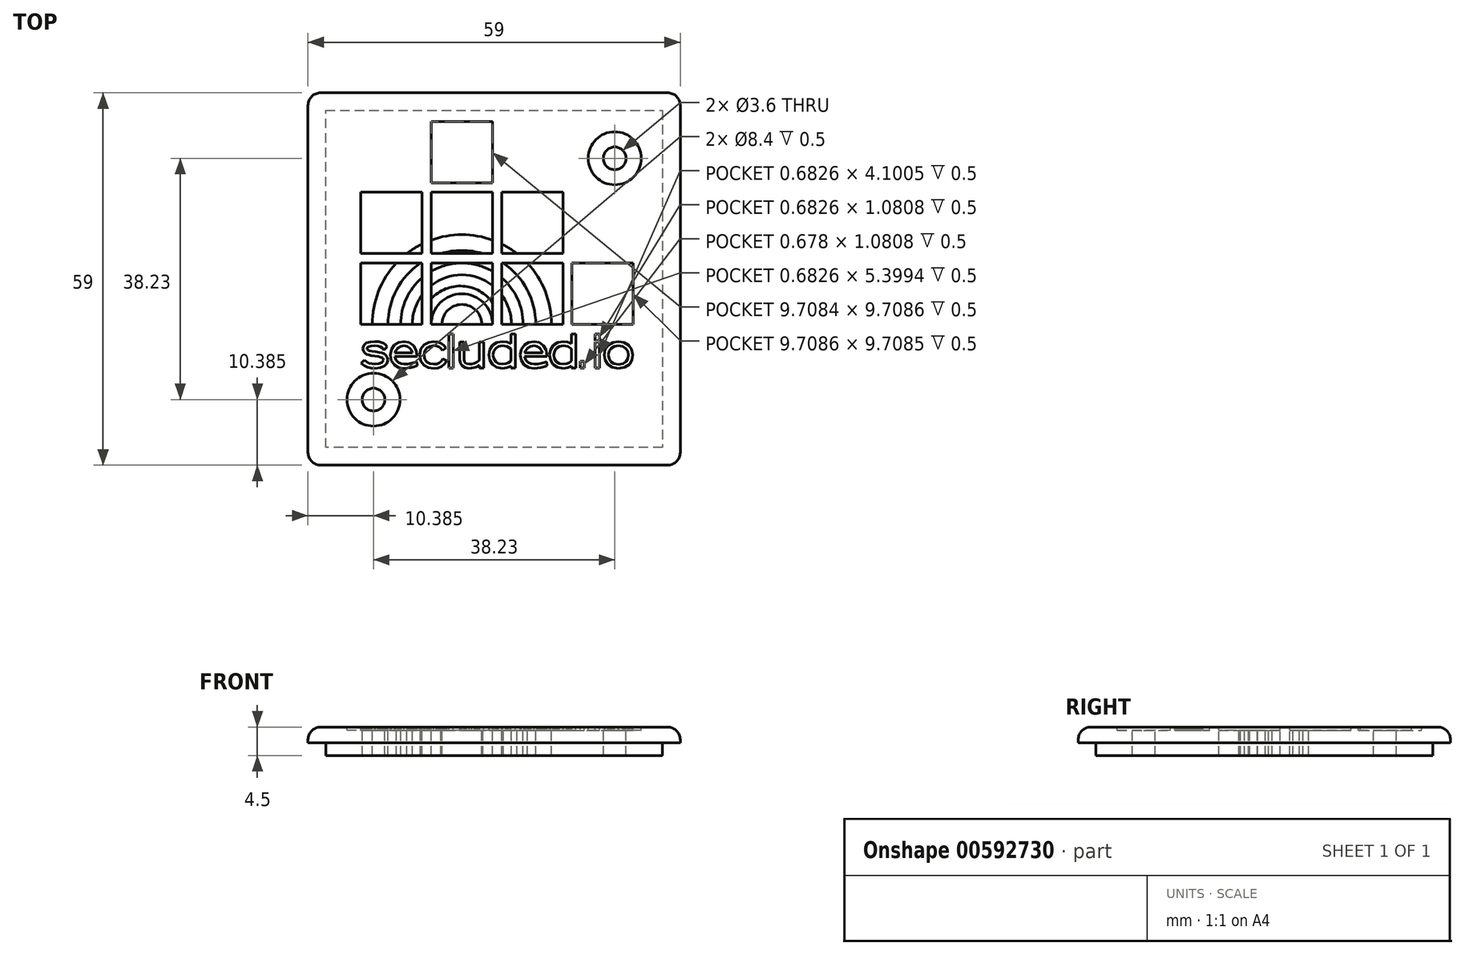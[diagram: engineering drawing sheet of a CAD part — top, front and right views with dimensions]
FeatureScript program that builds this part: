
annotation { "Feature Type Name" : "Feature", "Feature Type Description" : "" }
export const myFeature = defineFeature(function(context is Context, id is Id, definition is map)
    precondition{}
    {
        {
            var Q0;
            Q0=qCreatedBy(makeId("Top.planeOp"),FACE);
            var sketch = newSketch(context, id + "F0", { "sketchPlane" : qUnion([Q0])});
            skLineSegment(sketch, "E0.bottom", {"start": v(29.5, 29.5) * mm, "end": v(-29.5, 29.5) * mm});
            skLineSegment(sketch, "E0.top", {"start": v(29.5, -29.5) * mm, "end": v(-29.5, -29.5) * mm});
            skLineSegment(sketch, "E0.left", {"start": v(29.5, 29.5) * mm, "end": v(29.5, -29.5) * mm});
            skLineSegment(sketch, "E0.right", {"start": v(-29.5, 29.5) * mm, "end": v(-29.5, -29.5) * mm});
            skPoint(sketch, "E0.middle", {"position": v(0, 0) * mm});
            skLineSegment(sketch, "E1.bottom", {"start": v(23.88, -23.87) * mm, "end": v(-23.87, -23.88) * mm, "construction": true});
            skLineSegment(sketch, "E1.top", {"start": v(23.88, 23.88) * mm, "end": v(-23.88, 23.88) * mm, "construction": true});
            skLineSegment(sketch, "E1.left", {"start": v(23.88, -23.87) * mm, "end": v(23.88, 23.88) * mm, "construction": true});
            skLineSegment(sketch, "E1.right", {"start": v(-23.87, -23.88) * mm, "end": v(-23.88, 23.88) * mm, "construction": true});
            skSolve(sketch);
        }
        {
            var Q0;
            Q0=makeQuery(id+"F0.imprint","IMPRINT",FACE,{"disambiguationData":[TD([[makeQuery(id+"F0.imprint","IMPRINT",EDGE,{"derivedFrom":sQuery(id+"F0.wireOp",EDGE,"E0.bottom")}),1.0]])]});
            extrude(context, id + "F1", {"entities" : qUnion([Q0]), "depth" : 2.5 * mm, "offsetDistance" : 25 * mm});
        }
        {
            var Q0;
            Q0=makeQuery(id+"F1.opExtrude","CAP_FACE",FACE,{"disambiguationData":[OSD([sQuery(id+"F0.wireOp",EDGE,"E0.bottom"),sQuery(id+"F0.wireOp",EDGE,"E0.top"),sQuery(id+"F0.wireOp",EDGE,"E0.left"),sQuery(id+"F0.wireOp",EDGE,"E0.right")])],"isStart":true});
            var sketch = newSketch(context, id + "F2", { "sketchPlane" : qUnion([Q0])});
            skLineSegment(sketch, "E2.0", {"start": v(26.7, -26.7) * mm, "end": v(26.7, 26.7) * mm});
            skLineSegment(sketch, "E2.1", {"start": v(-26.7, -26.7) * mm, "end": v(26.7, -26.7) * mm});
            skLineSegment(sketch, "E2.2", {"start": v(-26.7, 26.7) * mm, "end": v(-26.7, -26.7) * mm});
            skLineSegment(sketch, "E2.3", {"start": v(26.7, 26.7) * mm, "end": v(-26.7, 26.7) * mm});
            skSolve(sketch);
        }
        {
            var Q0;
            Q0 = qSketchRegion(id + "F2", true);
            extrude(context, id + "F3", {"entities" : qUnion([Q0]), "operationType" : NewBodyOperationType.ADD, "depth" : 2 * mm, "offsetDistance" : 25 * mm});
        }
        {
            var Q0;
            Q0=makeQuery(id+"F1.opExtrude","CAP_FACE",FACE,{"disambiguationData":[OSD([sQuery(id+"F0.wireOp",EDGE,"E0.bottom"),sQuery(id+"F0.wireOp",EDGE,"E0.top"),sQuery(id+"F0.wireOp",EDGE,"E0.left"),sQuery(id+"F0.wireOp",EDGE,"E0.right")])],"isStart":false});
            var sketch = newSketch(context, id + "F4", { "sketchPlane" : qUnion([Q0])});
            skCircle(sketch, "E3", {"center": v(19.11, 19.12) * mm, "radius": 1.8 * mm});
            skCircle(sketch, "E4", {"center": v(-19.11, -19.11) * mm, "radius": 1.8 * mm});
            skSolve(sketch);
        }
        {
            var Q0;
            Q0 = qSketchRegion(id + "F4", true);
            extrude(context, id + "F5", {"entities" : qUnion([Q0]), "operationType" : NewBodyOperationType.REMOVE, "endBound" : BoundingType.THROUGH_ALL, "oppositeDirection" : true, "depth" : 25 * mm, "offsetDistance" : 25 * mm});
        }
        {
            var Q0;
            Q0=makeQuery(id+"F1.opExtrude","SWEPT_EDGE",EDGE,{"disambiguationData":[OSD([sQuery(id+"F0.wireOp",EDGE,"E0.top"),sQuery(id+"F0.wireOp",EDGE,"E0.right")])]});
            var Q1;
            Q1=makeQuery(id+"F1.opExtrude","SWEPT_EDGE",EDGE,{"disambiguationData":[OSD([sQuery(id+"F0.wireOp",EDGE,"E0.top"),sQuery(id+"F0.wireOp",EDGE,"E0.left")])]});
            var Q2;
            Q2=makeQuery(id+"F1.opExtrude","SWEPT_EDGE",EDGE,{"disambiguationData":[OSD([sQuery(id+"F0.wireOp",EDGE,"E0.bottom"),sQuery(id+"F0.wireOp",EDGE,"E0.left")])]});
            var Q3;
            Q3=makeQuery(id+"F1.opExtrude","SWEPT_EDGE",EDGE,{"disambiguationData":[OSD([sQuery(id+"F0.wireOp",EDGE,"E0.bottom"),sQuery(id+"F0.wireOp",EDGE,"E0.right")])]});
            fillet(context, id + "F6", {"entities" : qUnion([Q0, Q1, Q2, Q3]), "radius" : 2 * mm, "tangentPropagation" : true, "allowEdgeOverflow" : false});
        }
        {
            var Q0;
            Q0=makeQuery(id+"F1.opExtrude","CAP_EDGE",EDGE,{"disambiguationData":[OSD([sQuery(id+"F0.wireOp",EDGE,"E0.right")])],"isStart":false});
            fillet(context, id + "F7", {"entities" : qUnion([Q0]), "radius" : 2 * mm, "tangentPropagation" : true, "allowEdgeOverflow" : false});
        }
        {
            var Q0;
            Q0=makeQuery(id+"F1.opExtrude","CAP_FACE",FACE,{"disambiguationData":[OSD([sQuery(id+"F0.wireOp",EDGE,"E0.bottom"),sQuery(id+"F0.wireOp",EDGE,"E0.top"),sQuery(id+"F0.wireOp",EDGE,"E0.left"),sQuery(id+"F0.wireOp",EDGE,"E0.right")])],"isStart":false});
            var sketch = newSketch(context, id + "F8", { "sketchPlane" : qUnion([Q0])});
            skCircle(sketch, "E5", {"center": v(19.11, 19.12) * mm, "radius": 4.2 * mm});
            skCircle(sketch, "E6", {"center": v(-19.11, -19.11) * mm, "radius": 4.2 * mm});
            skSolve(sketch);
        }
        {
            var Q0;
            Q0 = qSketchRegion(id + "F8", true);
            extrude(context, id + "F9", {"entities" : qUnion([Q0]), "operationType" : NewBodyOperationType.REMOVE, "oppositeDirection" : true, "depth" : .5 * mm, "offsetDistance" : 25 * mm});
        }
        {
            var Q0;
            Q0=makeQuery(id+"F1.opExtrude","CAP_FACE",FACE,{"disambiguationData":[OSD([sQuery(id+"F0.wireOp",EDGE,"E0.bottom"),sQuery(id+"F0.wireOp",EDGE,"E0.top"),sQuery(id+"F0.wireOp",EDGE,"E0.left"),sQuery(id+"F0.wireOp",EDGE,"E0.right")])],"isStart":false});
            var sketch = newSketch(context, id + "F10", { "sketchPlane" : qUnion([Q0])});
            skLineSegment(sketch, "E7", {"start": v(-16.85, -12.84) * mm, "end": v(-16.95, -12.39) * mm});
            skLineSegment(sketch, "E8", {"start": v(-16.95, -12.39) * mm, "end": v(-17.23, -12.02) * mm});
            skLineSegment(sketch, "E9", {"start": v(-17.23, -12.02) * mm, "end": v(-17.48, -11.85) * mm});
            skLineSegment(sketch, "E10", {"start": v(-17.48, -11.85) * mm, "end": v(-17.8, -11.73) * mm});
            skLineSegment(sketch, "E11", {"start": v(-17.8, -11.73) * mm, "end": v(-18.23, -11.63) * mm});
            skLineSegment(sketch, "E12", {"start": v(-18.23, -11.63) * mm, "end": v(-18.78, -11.53) * mm});
            skLineSegment(sketch, "E13", {"start": v(-18.78, -11.53) * mm, "end": v(-19.36, -11.44) * mm});
            skLineSegment(sketch, "E14", {"start": v(-19.36, -11.44) * mm, "end": v(-19.71, -11.37) * mm});
            skLineSegment(sketch, "E15", {"start": v(-19.71, -11.37) * mm, "end": v(-19.9, -11.3) * mm});
            skLineSegment(sketch, "E16", {"start": v(-19.9, -11.3) * mm, "end": v(-20.03, -11.22) * mm});
            skLineSegment(sketch, "E17", {"start": v(-20.03, -11.22) * mm, "end": v(-20.12, -11.12) * mm});
            skLineSegment(sketch, "E18", {"start": v(-20.12, -11.12) * mm, "end": v(-20.14, -11.02) * mm});
            skLineSegment(sketch, "E19", {"start": v(-20.14, -11.02) * mm, "end": v(-20.1, -10.87) * mm});
            skLineSegment(sketch, "E20", {"start": v(-20.1, -10.87) * mm, "end": v(-19.93, -10.74) * mm});
            skLineSegment(sketch, "E21", {"start": v(-19.93, -10.74) * mm, "end": v(-19.48, -10.61) * mm});
            skLineSegment(sketch, "E22", {"start": v(-19.48, -10.61) * mm, "end": v(-18.9, -10.58) * mm});
            skLineSegment(sketch, "E23", {"start": v(-18.9, -10.58) * mm, "end": v(-18.4, -10.62) * mm});
            skLineSegment(sketch, "E24", {"start": v(-18.4, -10.62) * mm, "end": v(-18, -10.75) * mm});
            skLineSegment(sketch, "E25", {"start": v(-18, -10.75) * mm, "end": v(-17.7, -10.95) * mm});
            skLineSegment(sketch, "E26", {"start": v(-17.7, -10.95) * mm, "end": v(-17.46, -11.24) * mm});
            skLineSegment(sketch, "E27", {"start": v(-17.46, -11.24) * mm, "end": v(-16.92, -10.78) * mm});
            skLineSegment(sketch, "E28", {"start": v(-16.92, -10.78) * mm, "end": v(-17.15, -10.52) * mm});
            skLineSegment(sketch, "E29", {"start": v(-17.15, -10.52) * mm, "end": v(-17.35, -10.33) * mm});
            skLineSegment(sketch, "E30", {"start": v(-17.35, -10.33) * mm, "end": v(-17.54, -10.2) * mm});
            skLineSegment(sketch, "E31", {"start": v(-17.54, -10.2) * mm, "end": v(-17.72, -10.1) * mm});
            skLineSegment(sketch, "E32", {"start": v(-17.72, -10.1) * mm, "end": v(-18.3, -9.95) * mm});
            skLineSegment(sketch, "E33", {"start": v(-18.3, -9.95) * mm, "end": v(-18.9, -9.91) * mm});
            skLineSegment(sketch, "E34", {"start": v(-18.9, -9.91) * mm, "end": v(-19.63, -9.97) * mm});
            skLineSegment(sketch, "E35", {"start": v(-19.63, -9.97) * mm, "end": v(-20.22, -10.14) * mm});
            skLineSegment(sketch, "E36", {"start": v(-20.22, -10.14) * mm, "end": v(-20.67, -10.48) * mm});
            skLineSegment(sketch, "E37", {"start": v(-20.67, -10.48) * mm, "end": v(-20.83, -11.02) * mm});
            skLineSegment(sketch, "E38", {"start": v(-20.83, -11.02) * mm, "end": v(-20.72, -11.45) * mm});
            skLineSegment(sketch, "E39", {"start": v(-20.72, -11.45) * mm, "end": v(-20.41, -11.78) * mm});
            skLineSegment(sketch, "E40", {"start": v(-20.41, -11.78) * mm, "end": v(-20.17, -11.93) * mm});
            skLineSegment(sketch, "E41", {"start": v(-20.17, -11.93) * mm, "end": v(-19.87, -12.03) * mm});
            skLineSegment(sketch, "E42", {"start": v(-19.87, -12.03) * mm, "end": v(-19.47, -12.12) * mm});
            skLineSegment(sketch, "E43", {"start": v(-19.47, -12.12) * mm, "end": v(-18.92, -12.2) * mm});
            skLineSegment(sketch, "E44", {"start": v(-18.92, -12.2) * mm, "end": v(-18.36, -12.3) * mm});
            skLineSegment(sketch, "E45", {"start": v(-18.36, -12.3) * mm, "end": v(-18.02, -12.37) * mm});
            skLineSegment(sketch, "E46", {"start": v(-18.02, -12.37) * mm, "end": v(-17.8, -12.45) * mm});
            skLineSegment(sketch, "E47", {"start": v(-17.8, -12.45) * mm, "end": v(-17.67, -12.54) * mm});
            skLineSegment(sketch, "E48", {"start": v(-17.67, -12.54) * mm, "end": v(-17.56, -12.68) * mm});
            skLineSegment(sketch, "E49", {"start": v(-17.56, -12.68) * mm, "end": v(-17.53, -12.85) * mm});
            skLineSegment(sketch, "E50", {"start": v(-17.53, -12.85) * mm, "end": v(-17.77, -13.25) * mm});
            skLineSegment(sketch, "E51", {"start": v(-17.77, -13.25) * mm, "end": v(-18.26, -13.45) * mm});
            skLineSegment(sketch, "E52", {"start": v(-18.26, -13.45) * mm, "end": v(-18.86, -13.5) * mm});
            skLineSegment(sketch, "E53", {"start": v(-18.86, -13.5) * mm, "end": v(-19.86, -13.33) * mm});
            skLineSegment(sketch, "E54", {"start": v(-19.86, -13.33) * mm, "end": v(-20.57, -12.84) * mm});
            skLineSegment(sketch, "E55", {"start": v(-20.57, -12.84) * mm, "end": v(-21.07, -13.34) * mm});
            skLineSegment(sketch, "E56", {"start": v(-21.07, -13.34) * mm, "end": v(-20.79, -13.58) * mm});
            skLineSegment(sketch, "E57", {"start": v(-20.79, -13.58) * mm, "end": v(-20.54, -13.76) * mm});
            skLineSegment(sketch, "E58", {"start": v(-20.54, -13.76) * mm, "end": v(-20.3, -13.9) * mm});
            skLineSegment(sketch, "E59", {"start": v(-20.3, -13.9) * mm, "end": v(-20.06, -14) * mm});
            skLineSegment(sketch, "E60", {"start": v(-20.06, -14) * mm, "end": v(-19.5, -14.12) * mm});
            skLineSegment(sketch, "E61", {"start": v(-19.5, -14.12) * mm, "end": v(-18.84, -14.17) * mm});
            skLineSegment(sketch, "E62", {"start": v(-18.84, -14.17) * mm, "end": v(-18, -14.08) * mm});
            skLineSegment(sketch, "E63", {"start": v(-18, -14.08) * mm, "end": v(-17.38, -13.79) * mm});
            skLineSegment(sketch, "E64", {"start": v(-17.38, -13.79) * mm, "end": v(-16.99, -13.4) * mm});
            skLineSegment(sketch, "E65", {"start": v(-16.99, -13.4) * mm, "end": v(-16.85, -12.84) * mm});
            skLineSegment(sketch, "E66", {"start": v(-12.2, -12.3) * mm, "end": v(-12.35, -11.24) * mm});
            skLineSegment(sketch, "E67", {"start": v(-12.35, -11.24) * mm, "end": v(-12.76, -10.56) * mm});
            skLineSegment(sketch, "E68", {"start": v(-12.76, -10.56) * mm, "end": v(-13.44, -10.08) * mm});
            skLineSegment(sketch, "E69", {"start": v(-13.44, -10.08) * mm, "end": v(-14.26, -9.91) * mm});
            skLineSegment(sketch, "E70", {"start": v(-14.26, -9.91) * mm, "end": v(-15.11, -10.06) * mm});
            skLineSegment(sketch, "E71", {"start": v(-15.11, -10.06) * mm, "end": v(-15.79, -10.45) * mm});
            skLineSegment(sketch, "E72", {"start": v(-15.79, -10.45) * mm, "end": v(-16.27, -11.12) * mm});
            skLineSegment(sketch, "E73", {"start": v(-16.27, -11.12) * mm, "end": v(-16.45, -12) * mm});
            skLineSegment(sketch, "E74", {"start": v(-16.45, -12) * mm, "end": v(-16.28, -12.92) * mm});
            skLineSegment(sketch, "E75", {"start": v(-16.28, -12.92) * mm, "end": v(-15.83, -13.59) * mm});
            skLineSegment(sketch, "E76", {"start": v(-15.83, -13.59) * mm, "end": v(-15.1, -14.04) * mm});
            skLineSegment(sketch, "E77", {"start": v(-15.1, -14.04) * mm, "end": v(-14.26, -14.17) * mm});
            skLineSegment(sketch, "E78", {"start": v(-14.26, -14.17) * mm, "end": v(-13.76, -14.13) * mm});
            skLineSegment(sketch, "E79", {"start": v(-13.76, -14.13) * mm, "end": v(-13.22, -14.02) * mm});
            skLineSegment(sketch, "E80", {"start": v(-13.22, -14.02) * mm, "end": v(-12.72, -13.9) * mm});
            skLineSegment(sketch, "E81", {"start": v(-12.72, -13.9) * mm, "end": v(-12.36, -13.8) * mm});
            skLineSegment(sketch, "E82", {"start": v(-12.36, -13.8) * mm, "end": v(-12.21, -13.76) * mm});
            skLineSegment(sketch, "E83", {"start": v(-12.21, -13.76) * mm, "end": v(-12.26, -13.1) * mm});
            skLineSegment(sketch, "E84", {"start": v(-12.26, -13.1) * mm, "end": v(-12.61, -13.2) * mm});
            skLineSegment(sketch, "E85", {"start": v(-12.61, -13.2) * mm, "end": v(-13.12, -13.34) * mm});
            skLineSegment(sketch, "E86", {"start": v(-13.12, -13.34) * mm, "end": v(-13.7, -13.46) * mm});
            skLineSegment(sketch, "E87", {"start": v(-13.7, -13.46) * mm, "end": v(-14.27, -13.5) * mm});
            skLineSegment(sketch, "E88", {"start": v(-14.27, -13.5) * mm, "end": v(-14.76, -13.45) * mm});
            skLineSegment(sketch, "E89", {"start": v(-14.76, -13.45) * mm, "end": v(-15.2, -13.24) * mm});
            skLineSegment(sketch, "E90", {"start": v(-15.2, -13.24) * mm, "end": v(-15.55, -12.86) * mm});
            skLineSegment(sketch, "E91", {"start": v(-15.55, -12.86) * mm, "end": v(-15.74, -12.3) * mm});
            skLineSegment(sketch, "E92", {"start": v(-15.74, -12.3) * mm, "end": v(-12.2, -12.3) * mm});
            skLineSegment(sketch, "E93", {"start": v(-12.93, -11.72) * mm, "end": v(-15.74, -11.72) * mm});
            skLineSegment(sketch, "E94", {"start": v(-15.74, -11.72) * mm, "end": v(-15.57, -11.3) * mm});
            skLineSegment(sketch, "E95", {"start": v(-15.57, -11.3) * mm, "end": v(-15.25, -10.93) * mm});
            skLineSegment(sketch, "E96", {"start": v(-15.25, -10.93) * mm, "end": v(-14.8, -10.67) * mm});
            skLineSegment(sketch, "E97", {"start": v(-14.8, -10.67) * mm, "end": v(-14.26, -10.57) * mm});
            skLineSegment(sketch, "E98", {"start": v(-14.26, -10.57) * mm, "end": v(-13.78, -10.67) * mm});
            skLineSegment(sketch, "E99", {"start": v(-13.78, -10.67) * mm, "end": v(-13.39, -10.93) * mm});
            skLineSegment(sketch, "E100", {"start": v(-13.39, -10.93) * mm, "end": v(-13.1, -11.3) * mm});
            skLineSegment(sketch, "E101", {"start": v(-13.1, -11.3) * mm, "end": v(-12.93, -11.72) * mm});
            skLineSegment(sketch, "E102", {"start": v(-7.52, -12.98) * mm, "end": v(-8.13, -12.67) * mm});
            skLineSegment(sketch, "E103", {"start": v(-8.13, -12.67) * mm, "end": v(-8.4, -13.03) * mm});
            skLineSegment(sketch, "E104", {"start": v(-8.4, -13.03) * mm, "end": v(-8.7, -13.3) * mm});
            skLineSegment(sketch, "E105", {"start": v(-8.7, -13.3) * mm, "end": v(-9.08, -13.46) * mm});
            skLineSegment(sketch, "E106", {"start": v(-9.08, -13.46) * mm, "end": v(-9.56, -13.5) * mm});
            skLineSegment(sketch, "E107", {"start": v(-9.56, -13.5) * mm, "end": v(-10.15, -13.43) * mm});
            skLineSegment(sketch, "E108", {"start": v(-10.15, -13.43) * mm, "end": v(-10.66, -13.16) * mm});
            skLineSegment(sketch, "E109", {"start": v(-10.66, -13.16) * mm, "end": v(-11, -12.7) * mm});
            skLineSegment(sketch, "E110", {"start": v(-11, -12.7) * mm, "end": v(-11.13, -12.04) * mm});
            skLineSegment(sketch, "E111", {"start": v(-11.13, -12.04) * mm, "end": v(-11, -11.4) * mm});
            skLineSegment(sketch, "E112", {"start": v(-11, -11.4) * mm, "end": v(-10.66, -10.94) * mm});
            skLineSegment(sketch, "E113", {"start": v(-10.66, -10.94) * mm, "end": v(-10.15, -10.66) * mm});
            skLineSegment(sketch, "E114", {"start": v(-10.15, -10.66) * mm, "end": v(-9.56, -10.57) * mm});
            skLineSegment(sketch, "E115", {"start": v(-9.56, -10.57) * mm, "end": v(-9.12, -10.62) * mm});
            skLineSegment(sketch, "E116", {"start": v(-9.12, -10.62) * mm, "end": v(-8.78, -10.74) * mm});
            skLineSegment(sketch, "E117", {"start": v(-8.78, -10.74) * mm, "end": v(-8.48, -10.96) * mm});
            skLineSegment(sketch, "E118", {"start": v(-8.48, -10.96) * mm, "end": v(-8.2, -11.3) * mm});
            skLineSegment(sketch, "E119", {"start": v(-8.2, -11.3) * mm, "end": v(-7.62, -10.95) * mm});
            skLineSegment(sketch, "E120", {"start": v(-7.62, -10.95) * mm, "end": v(-8.03, -10.48) * mm});
            skLineSegment(sketch, "E121", {"start": v(-8.03, -10.48) * mm, "end": v(-8.47, -10.16) * mm});
            skLineSegment(sketch, "E122", {"start": v(-8.47, -10.16) * mm, "end": v(-8.96, -9.97) * mm});
            skLineSegment(sketch, "E123", {"start": v(-8.96, -9.97) * mm, "end": v(-9.56, -9.91) * mm});
            skLineSegment(sketch, "E124", {"start": v(-9.56, -9.91) * mm, "end": v(-10.38, -10.04) * mm});
            skLineSegment(sketch, "E125", {"start": v(-10.38, -10.04) * mm, "end": v(-11.1, -10.43) * mm});
            skLineSegment(sketch, "E126", {"start": v(-11.1, -10.43) * mm, "end": v(-11.62, -11.1) * mm});
            skLineSegment(sketch, "E127", {"start": v(-11.62, -11.1) * mm, "end": v(-11.81, -12.04) * mm});
            skLineSegment(sketch, "E128", {"start": v(-11.81, -12.04) * mm, "end": v(-11.62, -13) * mm});
            skLineSegment(sketch, "E129", {"start": v(-11.62, -13) * mm, "end": v(-11.11, -13.67) * mm});
            skLineSegment(sketch, "E130", {"start": v(-11.11, -13.67) * mm, "end": v(-10.39, -14.05) * mm});
            skLineSegment(sketch, "E131", {"start": v(-10.39, -14.05) * mm, "end": v(-9.56, -14.17) * mm});
            skLineSegment(sketch, "E132", {"start": v(-9.56, -14.17) * mm, "end": v(-8.87, -14.09) * mm});
            skLineSegment(sketch, "E133", {"start": v(-8.87, -14.09) * mm, "end": v(-8.32, -13.85) * mm});
            skLineSegment(sketch, "E134", {"start": v(-8.32, -13.85) * mm, "end": v(-7.89, -13.48) * mm});
            skLineSegment(sketch, "E135", {"start": v(-7.89, -13.48) * mm, "end": v(-7.52, -12.98) * mm});
            skLineSegment(sketch, "E136", {"start": v(-7.18, -8.7) * mm, "end": v(-6.5, -8.7) * mm});
            skLineSegment(sketch, "E137", {"start": v(-6.5, -8.7) * mm, "end": v(-6.5, -14.1) * mm});
            skLineSegment(sketch, "E138", {"start": v(-6.5, -14.1) * mm, "end": v(-7.18, -14.1) * mm});
            skLineSegment(sketch, "E139", {"start": v(-7.18, -14.1) * mm, "end": v(-7.18, -8.7) * mm});
            skLineSegment(sketch, "E140", {"start": v(-1.64, -14.1) * mm, "end": v(-1.64, -13.25) * mm});
            skLineSegment(sketch, "E141", {"start": v(-2.33, -10) * mm, "end": v(-1.64, -10) * mm});
            skLineSegment(sketch, "E142", {"start": v(-2.33, -10) * mm, "end": v(-2.33, -12.88) * mm});
            skLineSegment(sketch, "E143", {"start": v(-2.33, -12.88) * mm, "end": v(-2.76, -13.16) * mm});
            skLineSegment(sketch, "E144", {"start": v(-2.76, -13.16) * mm, "end": v(-3.13, -13.34) * mm});
            skLineSegment(sketch, "E145", {"start": v(-3.13, -13.34) * mm, "end": v(-3.54, -13.47) * mm});
            skLineSegment(sketch, "E146", {"start": v(-3.54, -13.47) * mm, "end": v(-3.91, -13.5) * mm});
            skLineSegment(sketch, "E147", {"start": v(-3.91, -13.5) * mm, "end": v(-4.37, -13.44) * mm});
            skLineSegment(sketch, "E148", {"start": v(-4.37, -13.44) * mm, "end": v(-4.6, -13.3) * mm});
            skLineSegment(sketch, "E149", {"start": v(-4.6, -13.3) * mm, "end": v(-4.72, -13.08) * mm});
            skLineSegment(sketch, "E150", {"start": v(-4.72, -13.08) * mm, "end": v(-4.75, -12.76) * mm});
            skLineSegment(sketch, "E151", {"start": v(-4.75, -12.76) * mm, "end": v(-4.75, -10) * mm});
            skLineSegment(sketch, "E152", {"start": v(-4.75, -10) * mm, "end": v(-5.44, -10) * mm});
            skLineSegment(sketch, "E153", {"start": v(-5.44, -10) * mm, "end": v(-5.44, -12.77) * mm});
            skLineSegment(sketch, "E154", {"start": v(-5.44, -12.77) * mm, "end": v(-5.35, -13.33) * mm});
            skLineSegment(sketch, "E155", {"start": v(-5.35, -13.33) * mm, "end": v(-5.08, -13.76) * mm});
            skLineSegment(sketch, "E156", {"start": v(-5.08, -13.76) * mm, "end": v(-4.58, -14.07) * mm});
            skLineSegment(sketch, "E157", {"start": v(-4.58, -14.07) * mm, "end": v(-3.93, -14.17) * mm});
            skLineSegment(sketch, "E158", {"start": v(-3.93, -14.17) * mm, "end": v(-2.91, -13.96) * mm});
            skLineSegment(sketch, "E159", {"start": v(-2.91, -13.96) * mm, "end": v(-2.61, -13.83) * mm});
            skLineSegment(sketch, "E160", {"start": v(-2.61, -13.83) * mm, "end": v(-2.32, -13.67) * mm});
            skLineSegment(sketch, "E161", {"start": v(-2.32, -13.67) * mm, "end": v(-2.32, -13.85) * mm});
            skLineSegment(sketch, "E162", {"start": v(-2.32, -13.85) * mm, "end": v(-2.33, -14.02) * mm});
            skLineSegment(sketch, "E163", {"start": v(-2.33, -14.02) * mm, "end": v(-2.33, -14.1) * mm});
            skLineSegment(sketch, "E164", {"start": v(-2.33, -14.1) * mm, "end": v(-1.64, -14.1) * mm});
            skLineSegment(sketch, "E165", {"start": v(3.34, -14.1) * mm, "end": v(3.34, -8.7) * mm});
            skLineSegment(sketch, "E166", {"start": v(3.34, -8.7) * mm, "end": v(2.66, -8.7) * mm});
            skLineSegment(sketch, "E167", {"start": v(2.66, -8.7) * mm, "end": v(2.66, -10.27) * mm});
            skLineSegment(sketch, "E168", {"start": v(2.66, -10.27) * mm, "end": v(2.03, -10) * mm});
            skLineSegment(sketch, "E169", {"start": v(2.03, -10) * mm, "end": v(1.35, -9.91) * mm});
            skLineSegment(sketch, "E170", {"start": v(1.35, -9.91) * mm, "end": v(0.45, -10.08) * mm});
            skLineSegment(sketch, "E171", {"start": v(0.45, -10.08) * mm, "end": v(-0.24, -10.52) * mm});
            skLineSegment(sketch, "E172", {"start": v(-0.24, -10.52) * mm, "end": v(-0.68, -11.2) * mm});
            skLineSegment(sketch, "E173", {"start": v(-0.68, -11.2) * mm, "end": v(-0.84, -12.04) * mm});
            skLineSegment(sketch, "E174", {"start": v(-0.84, -12.04) * mm, "end": v(-0.7, -12.83) * mm});
            skLineSegment(sketch, "E175", {"start": v(-0.7, -12.83) * mm, "end": v(-0.28, -13.51) * mm});
            skLineSegment(sketch, "E176", {"start": v(-0.28, -13.51) * mm, "end": v(0.4, -14) * mm});
            skLineSegment(sketch, "E177", {"start": v(0.4, -14) * mm, "end": v(1.36, -14.17) * mm});
            skLineSegment(sketch, "E178", {"start": v(1.36, -14.17) * mm, "end": v(2.04, -14.08) * mm});
            skLineSegment(sketch, "E179", {"start": v(2.04, -14.08) * mm, "end": v(2.66, -13.8) * mm});
            skLineSegment(sketch, "E180", {"start": v(2.66, -13.8) * mm, "end": v(2.66, -13.92) * mm});
            skLineSegment(sketch, "E181", {"start": v(2.66, -13.92) * mm, "end": v(2.65, -14.04) * mm});
            skLineSegment(sketch, "E182", {"start": v(2.65, -14.04) * mm, "end": v(2.65, -14.1) * mm});
            skLineSegment(sketch, "E183", {"start": v(2.65, -14.1) * mm, "end": v(3.34, -14.1) * mm});
            skLineSegment(sketch, "E184", {"start": v(2.66, -12.98) * mm, "end": v(2.6, -13.04) * mm});
            skLineSegment(sketch, "E185", {"start": v(2.6, -13.04) * mm, "end": v(2.53, -13.1) * mm});
            skLineSegment(sketch, "E186", {"start": v(2.53, -13.1) * mm, "end": v(2.24, -13.3) * mm});
            skLineSegment(sketch, "E187", {"start": v(2.24, -13.3) * mm, "end": v(1.87, -13.45) * mm});
            skLineSegment(sketch, "E188", {"start": v(1.87, -13.45) * mm, "end": v(1.36, -13.5) * mm});
            skLineSegment(sketch, "E189", {"start": v(1.36, -13.5) * mm, "end": v(0.7, -13.4) * mm});
            skLineSegment(sketch, "E190", {"start": v(0.7, -13.4) * mm, "end": v(0.23, -13.07) * mm});
            skLineSegment(sketch, "E191", {"start": v(0.23, -13.07) * mm, "end": v(-0.06, -12.6) * mm});
            skLineSegment(sketch, "E192", {"start": v(-0.06, -12.6) * mm, "end": v(-0.16, -12.04) * mm});
            skLineSegment(sketch, "E193", {"start": v(-0.16, -12.04) * mm, "end": v(-0.06, -11.47) * mm});
            skLineSegment(sketch, "E194", {"start": v(-0.06, -11.47) * mm, "end": v(0.24, -11) * mm});
            skLineSegment(sketch, "E195", {"start": v(0.24, -11) * mm, "end": v(0.7, -10.69) * mm});
            skLineSegment(sketch, "E196", {"start": v(0.7, -10.69) * mm, "end": v(1.36, -10.57) * mm});
            skLineSegment(sketch, "E197", {"start": v(1.36, -10.57) * mm, "end": v(2.04, -10.69) * mm});
            skLineSegment(sketch, "E198", {"start": v(2.04, -10.69) * mm, "end": v(2.66, -11.1) * mm});
            skLineSegment(sketch, "E199", {"start": v(2.66, -11.1) * mm, "end": v(2.66, -12.98) * mm});
            skLineSegment(sketch, "E200", {"start": v(8.4, -12.3) * mm, "end": v(8.25, -11.24) * mm});
            skLineSegment(sketch, "E201", {"start": v(8.25, -11.24) * mm, "end": v(7.84, -10.56) * mm});
            skLineSegment(sketch, "E202", {"start": v(7.84, -10.56) * mm, "end": v(7.16, -10.08) * mm});
            skLineSegment(sketch, "E203", {"start": v(7.16, -10.08) * mm, "end": v(6.34, -9.91) * mm});
            skLineSegment(sketch, "E204", {"start": v(6.34, -9.91) * mm, "end": v(5.49, -10.06) * mm});
            skLineSegment(sketch, "E205", {"start": v(5.49, -10.06) * mm, "end": v(4.81, -10.45) * mm});
            skLineSegment(sketch, "E206", {"start": v(4.81, -10.45) * mm, "end": v(4.33, -11.12) * mm});
            skLineSegment(sketch, "E207", {"start": v(4.33, -11.12) * mm, "end": v(4.15, -12) * mm});
            skLineSegment(sketch, "E208", {"start": v(4.15, -12) * mm, "end": v(4.32, -12.92) * mm});
            skLineSegment(sketch, "E209", {"start": v(4.32, -12.92) * mm, "end": v(4.77, -13.59) * mm});
            skLineSegment(sketch, "E210", {"start": v(4.77, -13.59) * mm, "end": v(5.5, -14.04) * mm});
            skLineSegment(sketch, "E211", {"start": v(5.5, -14.04) * mm, "end": v(6.34, -14.17) * mm});
            skLineSegment(sketch, "E212", {"start": v(6.34, -14.17) * mm, "end": v(6.84, -14.13) * mm});
            skLineSegment(sketch, "E213", {"start": v(6.84, -14.13) * mm, "end": v(7.38, -14.02) * mm});
            skLineSegment(sketch, "E214", {"start": v(7.38, -14.02) * mm, "end": v(7.88, -13.9) * mm});
            skLineSegment(sketch, "E215", {"start": v(7.88, -13.9) * mm, "end": v(8.24, -13.8) * mm});
            skLineSegment(sketch, "E216", {"start": v(8.24, -13.8) * mm, "end": v(8.39, -13.76) * mm});
            skLineSegment(sketch, "E217", {"start": v(8.39, -13.76) * mm, "end": v(8.34, -13.1) * mm});
            skLineSegment(sketch, "E218", {"start": v(8.34, -13.1) * mm, "end": v(7.98, -13.2) * mm});
            skLineSegment(sketch, "E219", {"start": v(7.98, -13.2) * mm, "end": v(7.48, -13.34) * mm});
            skLineSegment(sketch, "E220", {"start": v(7.48, -13.34) * mm, "end": v(6.9, -13.46) * mm});
            skLineSegment(sketch, "E221", {"start": v(6.9, -13.46) * mm, "end": v(6.33, -13.5) * mm});
            skLineSegment(sketch, "E222", {"start": v(6.33, -13.5) * mm, "end": v(5.84, -13.45) * mm});
            skLineSegment(sketch, "E223", {"start": v(5.84, -13.45) * mm, "end": v(5.4, -13.24) * mm});
            skLineSegment(sketch, "E224", {"start": v(5.4, -13.24) * mm, "end": v(5.05, -12.86) * mm});
            skLineSegment(sketch, "E225", {"start": v(5.05, -12.86) * mm, "end": v(4.86, -12.3) * mm});
            skLineSegment(sketch, "E226", {"start": v(4.86, -12.3) * mm, "end": v(8.4, -12.3) * mm});
            skLineSegment(sketch, "E227", {"start": v(7.67, -11.72) * mm, "end": v(4.86, -11.72) * mm});
            skLineSegment(sketch, "E228", {"start": v(4.86, -11.72) * mm, "end": v(5.03, -11.3) * mm});
            skLineSegment(sketch, "E229", {"start": v(5.03, -11.3) * mm, "end": v(5.35, -10.93) * mm});
            skLineSegment(sketch, "E230", {"start": v(5.35, -10.93) * mm, "end": v(5.8, -10.67) * mm});
            skLineSegment(sketch, "E231", {"start": v(5.8, -10.67) * mm, "end": v(6.34, -10.57) * mm});
            skLineSegment(sketch, "E232", {"start": v(6.34, -10.57) * mm, "end": v(6.82, -10.67) * mm});
            skLineSegment(sketch, "E233", {"start": v(6.82, -10.67) * mm, "end": v(7.21, -10.93) * mm});
            skLineSegment(sketch, "E234", {"start": v(7.21, -10.93) * mm, "end": v(7.5, -11.3) * mm});
            skLineSegment(sketch, "E235", {"start": v(7.5, -11.3) * mm, "end": v(7.67, -11.72) * mm});
            skLineSegment(sketch, "E236", {"start": v(12.96, -14.1) * mm, "end": v(12.96, -8.7) * mm});
            skLineSegment(sketch, "E237", {"start": v(12.96, -8.7) * mm, "end": v(12.29, -8.7) * mm});
            skLineSegment(sketch, "E238", {"start": v(12.29, -8.7) * mm, "end": v(12.29, -10.27) * mm});
            skLineSegment(sketch, "E239", {"start": v(12.29, -10.27) * mm, "end": v(11.65, -10) * mm});
            skLineSegment(sketch, "E240", {"start": v(11.65, -10) * mm, "end": v(10.98, -9.91) * mm});
            skLineSegment(sketch, "E241", {"start": v(10.98, -9.91) * mm, "end": v(10.07, -10.08) * mm});
            skLineSegment(sketch, "E242", {"start": v(10.07, -10.08) * mm, "end": v(9.38, -10.52) * mm});
            skLineSegment(sketch, "E243", {"start": v(9.38, -10.52) * mm, "end": v(8.94, -11.2) * mm});
            skLineSegment(sketch, "E244", {"start": v(8.94, -11.2) * mm, "end": v(8.79, -12.04) * mm});
            skLineSegment(sketch, "E245", {"start": v(8.79, -12.04) * mm, "end": v(8.92, -12.83) * mm});
            skLineSegment(sketch, "E246", {"start": v(8.92, -12.83) * mm, "end": v(9.34, -13.51) * mm});
            skLineSegment(sketch, "E247", {"start": v(9.34, -13.51) * mm, "end": v(10.03, -14) * mm});
            skLineSegment(sketch, "E248", {"start": v(10.03, -14) * mm, "end": v(10.99, -14.17) * mm});
            skLineSegment(sketch, "E249", {"start": v(10.99, -14.17) * mm, "end": v(11.66, -14.08) * mm});
            skLineSegment(sketch, "E250", {"start": v(11.66, -14.08) * mm, "end": v(12.29, -13.8) * mm});
            skLineSegment(sketch, "E251", {"start": v(12.29, -13.8) * mm, "end": v(12.28, -13.92) * mm});
            skLineSegment(sketch, "E252", {"start": v(12.28, -13.92) * mm, "end": v(12.28, -14.04) * mm});
            skLineSegment(sketch, "E253", {"start": v(12.28, -14.04) * mm, "end": v(12.28, -14.1) * mm});
            skLineSegment(sketch, "E254", {"start": v(12.28, -14.1) * mm, "end": v(12.96, -14.1) * mm});
            skLineSegment(sketch, "E255", {"start": v(12.29, -12.98) * mm, "end": v(12.22, -13.04) * mm});
            skLineSegment(sketch, "E256", {"start": v(12.22, -13.04) * mm, "end": v(12.15, -13.1) * mm});
            skLineSegment(sketch, "E257", {"start": v(12.15, -13.1) * mm, "end": v(11.86, -13.3) * mm});
            skLineSegment(sketch, "E258", {"start": v(11.86, -13.3) * mm, "end": v(11.49, -13.45) * mm});
            skLineSegment(sketch, "E259", {"start": v(11.49, -13.45) * mm, "end": v(10.99, -13.5) * mm});
            skLineSegment(sketch, "E260", {"start": v(10.99, -13.5) * mm, "end": v(10.33, -13.4) * mm});
            skLineSegment(sketch, "E261", {"start": v(10.33, -13.4) * mm, "end": v(9.85, -13.07) * mm});
            skLineSegment(sketch, "E262", {"start": v(9.85, -13.07) * mm, "end": v(9.56, -12.6) * mm});
            skLineSegment(sketch, "E263", {"start": v(9.56, -12.6) * mm, "end": v(9.47, -12.04) * mm});
            skLineSegment(sketch, "E264", {"start": v(9.47, -12.04) * mm, "end": v(9.56, -11.47) * mm});
            skLineSegment(sketch, "E265", {"start": v(9.56, -11.47) * mm, "end": v(9.86, -11) * mm});
            skLineSegment(sketch, "E266", {"start": v(9.86, -11) * mm, "end": v(10.33, -10.69) * mm});
            skLineSegment(sketch, "E267", {"start": v(10.33, -10.69) * mm, "end": v(10.98, -10.57) * mm});
            skLineSegment(sketch, "E268", {"start": v(10.98, -10.57) * mm, "end": v(11.66, -10.69) * mm});
            skLineSegment(sketch, "E269", {"start": v(11.66, -10.69) * mm, "end": v(12.29, -11.1) * mm});
            skLineSegment(sketch, "E270", {"start": v(12.29, -11.1) * mm, "end": v(12.29, -12.98) * mm});
            skLineSegment(sketch, "E271", {"start": v(13.63, -13.01) * mm, "end": v(14.3, -13.01) * mm});
            skLineSegment(sketch, "E272", {"start": v(14.3, -13.01) * mm, "end": v(14.3, -14.1) * mm});
            skLineSegment(sketch, "E273", {"start": v(14.3, -14.1) * mm, "end": v(13.63, -14.1) * mm});
            skLineSegment(sketch, "E274", {"start": v(13.63, -14.1) * mm, "end": v(13.63, -13.01) * mm});
            skLineSegment(sketch, "E275", {"start": v(16.67, -9.77) * mm, "end": v(16.67, -8.7) * mm});
            skLineSegment(sketch, "E276", {"start": v(16.67, -8.7) * mm, "end": v(15.99, -8.7) * mm});
            skLineSegment(sketch, "E277", {"start": v(15.99, -8.7) * mm, "end": v(15.99, -9.77) * mm});
            skLineSegment(sketch, "E278", {"start": v(15.99, -9.77) * mm, "end": v(16.67, -9.77) * mm});
            skLineSegment(sketch, "E279", {"start": v(16.67, -14.1) * mm, "end": v(16.67, -10) * mm});
            skLineSegment(sketch, "E280", {"start": v(16.67, -10) * mm, "end": v(15.99, -10) * mm});
            skLineSegment(sketch, "E281", {"start": v(15.99, -10) * mm, "end": v(15.99, -14.1) * mm});
            skLineSegment(sketch, "E282", {"start": v(15.99, -14.1) * mm, "end": v(16.67, -14.1) * mm});
            skLineSegment(sketch, "E283", {"start": v(21.99, -12.05) * mm, "end": v(21.8, -11.14) * mm});
            skLineSegment(sketch, "E284", {"start": v(21.8, -11.14) * mm, "end": v(21.32, -10.48) * mm});
            skLineSegment(sketch, "E285", {"start": v(21.32, -10.48) * mm, "end": v(20.59, -10.06) * mm});
            skLineSegment(sketch, "E286", {"start": v(20.59, -10.06) * mm, "end": v(19.72, -9.91) * mm});
            skLineSegment(sketch, "E287", {"start": v(19.72, -9.91) * mm, "end": v(18.84, -10.06) * mm});
            skLineSegment(sketch, "E288", {"start": v(18.84, -10.06) * mm, "end": v(18.12, -10.47) * mm});
            skLineSegment(sketch, "E289", {"start": v(18.12, -10.47) * mm, "end": v(17.62, -11.14) * mm});
            skLineSegment(sketch, "E290", {"start": v(17.62, -11.14) * mm, "end": v(17.44, -12.04) * mm});
            skLineSegment(sketch, "E291", {"start": v(17.44, -12.04) * mm, "end": v(17.58, -12.85) * mm});
            skLineSegment(sketch, "E292", {"start": v(17.58, -12.85) * mm, "end": v(18.01, -13.53) * mm});
            skLineSegment(sketch, "E293", {"start": v(18.01, -13.53) * mm, "end": v(18.72, -14) * mm});
            skLineSegment(sketch, "E294", {"start": v(18.72, -14) * mm, "end": v(19.72, -14.17) * mm});
            skLineSegment(sketch, "E295", {"start": v(19.72, -14.17) * mm, "end": v(20.72, -14) * mm});
            skLineSegment(sketch, "E296", {"start": v(20.72, -14) * mm, "end": v(21.43, -13.51) * mm});
            skLineSegment(sketch, "E297", {"start": v(21.43, -13.51) * mm, "end": v(21.85, -12.83) * mm});
            skLineSegment(sketch, "E298", {"start": v(21.85, -12.83) * mm, "end": v(21.99, -12.05) * mm});
            skLineSegment(sketch, "E299", {"start": v(21.3, -12.05) * mm, "end": v(21.21, -12.6) * mm});
            skLineSegment(sketch, "E300", {"start": v(21.21, -12.6) * mm, "end": v(20.92, -13.07) * mm});
            skLineSegment(sketch, "E301", {"start": v(20.92, -13.07) * mm, "end": v(20.43, -13.4) * mm});
            skLineSegment(sketch, "E302", {"start": v(20.43, -13.4) * mm, "end": v(19.72, -13.52) * mm});
            skLineSegment(sketch, "E303", {"start": v(19.72, -13.52) * mm, "end": v(19, -13.4) * mm});
            skLineSegment(sketch, "E304", {"start": v(19, -13.4) * mm, "end": v(18.5, -13.07) * mm});
            skLineSegment(sketch, "E305", {"start": v(18.5, -13.07) * mm, "end": v(18.21, -12.6) * mm});
            skLineSegment(sketch, "E306", {"start": v(18.21, -12.6) * mm, "end": v(18.12, -12.05) * mm});
            skLineSegment(sketch, "E307", {"start": v(18.12, -12.05) * mm, "end": v(18.24, -11.44) * mm});
            skLineSegment(sketch, "E308", {"start": v(18.24, -11.44) * mm, "end": v(18.57, -10.97) * mm});
            skLineSegment(sketch, "E309", {"start": v(18.57, -10.97) * mm, "end": v(19.07, -10.68) * mm});
            skLineSegment(sketch, "E310", {"start": v(19.07, -10.68) * mm, "end": v(19.72, -10.58) * mm});
            skLineSegment(sketch, "E311", {"start": v(19.72, -10.58) * mm, "end": v(20.36, -10.68) * mm});
            skLineSegment(sketch, "E312", {"start": v(20.36, -10.68) * mm, "end": v(20.86, -10.97) * mm});
            skLineSegment(sketch, "E313", {"start": v(20.86, -10.97) * mm, "end": v(21.19, -11.44) * mm});
            skLineSegment(sketch, "E314", {"start": v(21.19, -11.44) * mm, "end": v(21.3, -12.05) * mm});
            skLineSegment(sketch, "E315", {"start": v(-21.12, 2.51) * mm, "end": v(-11.41, 2.51) * mm});
            skLineSegment(sketch, "E316", {"start": v(-11.41, 2.51) * mm, "end": v(-11.41, -7.2) * mm});
            skLineSegment(sketch, "E317", {"start": v(-11.41, -7.2) * mm, "end": v(-21.12, -7.2) * mm});
            skLineSegment(sketch, "E318", {"start": v(-21.12, -7.2) * mm, "end": v(-21.12, 2.51) * mm});
            skLineSegment(sketch, "E319", {"start": v(-9.96, 2.51) * mm, "end": v(-0.15, 2.51) * mm});
            skLineSegment(sketch, "E320", {"start": v(-0.26, 2.51) * mm, "end": v(-0.26, -7.2) * mm});
            skLineSegment(sketch, "E321", {"start": v(-0.26, -7.2) * mm, "end": v(-9.96, -7.2) * mm});
            skLineSegment(sketch, "E322", {"start": v(-9.96, -7.2) * mm, "end": v(-9.96, 2.51) * mm});
            skLineSegment(sketch, "E323", {"start": v(1.2, 2.51) * mm, "end": v(10.9, 2.51) * mm});
            skLineSegment(sketch, "E324", {"start": v(10.9, 2.51) * mm, "end": v(10.9, -7.2) * mm});
            skLineSegment(sketch, "E325", {"start": v(10.9, -7.2) * mm, "end": v(1.2, -7.2) * mm});
            skLineSegment(sketch, "E326", {"start": v(1.2, -7.2) * mm, "end": v(1.2, 2.51) * mm});
            skLineSegment(sketch, "E327", {"start": v(12.35, 2.51) * mm, "end": v(22.06, 2.51) * mm});
            skLineSegment(sketch, "E328", {"start": v(22.06, 2.51) * mm, "end": v(22.06, -7.2) * mm});
            skLineSegment(sketch, "E329", {"start": v(22.06, -7.2) * mm, "end": v(12.35, -7.2) * mm});
            skLineSegment(sketch, "E330", {"start": v(12.35, -7.2) * mm, "end": v(12.35, 2.51) * mm});
            skLineSegment(sketch, "E331", {"start": v(-9.96, 13.74) * mm, "end": v(-0.26, 13.74) * mm});
            skLineSegment(sketch, "E332", {"start": v(-0.26, 13.74) * mm, "end": v(-0.26, 4.03) * mm});
            skLineSegment(sketch, "E333", {"start": v(-0.26, 4.03) * mm, "end": v(-9.96, 4.03) * mm});
            skLineSegment(sketch, "E334", {"start": v(-9.96, 4.03) * mm, "end": v(-9.96, 13.74) * mm});
            skLineSegment(sketch, "E335", {"start": v(1.2, 13.74) * mm, "end": v(10.9, 13.74) * mm});
            skLineSegment(sketch, "E336", {"start": v(10.9, 13.74) * mm, "end": v(10.9, 4.03) * mm});
            skLineSegment(sketch, "E337", {"start": v(10.9, 4.03) * mm, "end": v(1.2, 4.03) * mm});
            skLineSegment(sketch, "E338", {"start": v(1.2, 4.03) * mm, "end": v(1.2, 13.74) * mm});
            skLineSegment(sketch, "E339", {"start": v(-21.12, 13.74) * mm, "end": v(-11.41, 13.74) * mm});
            skLineSegment(sketch, "E340", {"start": v(-11.41, 13.74) * mm, "end": v(-11.41, 4.03) * mm});
            skLineSegment(sketch, "E341", {"start": v(-11.41, 4.03) * mm, "end": v(-21.12, 4.03) * mm});
            skLineSegment(sketch, "E342", {"start": v(-21.12, 4.03) * mm, "end": v(-21.12, 13.74) * mm});
            skLineSegment(sketch, "E343", {"start": v(-9.96, 24.9) * mm, "end": v(-0.26, 24.9) * mm});
            skLineSegment(sketch, "E344", {"start": v(-0.26, 24.9) * mm, "end": v(-0.26, 15.2) * mm});
            skLineSegment(sketch, "E345", {"start": v(-0.26, 15.2) * mm, "end": v(-9.96, 15.2) * mm});
            skLineSegment(sketch, "E346", {"start": v(-9.96, 15.2) * mm, "end": v(-9.96, 24.9) * mm});
            skLineSegment(sketch, "E347", {"start": v(-1.64, -10) * mm, "end": v(-1.64, -13.25) * mm});
            skSolve(sketch);
        }
        {
            var Q0;
            Q0 = qSketchRegion(id + "F10", true);
            extrude(context, id + "F11", {"entities" : qUnion([Q0]), "operationType" : NewBodyOperationType.REMOVE, "oppositeDirection" : true, "depth" : .5 * mm, "offsetDistance" : 25 * mm});
        }
        {
            var Q0;
            Q0=makeQuery(id+"F11.boolean.opBoolean","COPY",FACE,{"derivedFrom":makeQuery(id+"F11.opExtrude","CAP_FACE",FACE,{"disambiguationData":[OSD([sQuery(id+"F10.wireOp",EDGE,"E319"),sQuery(id+"F10.wireOp",EDGE,"E320"),sQuery(id+"F10.wireOp",EDGE,"E321"),sQuery(id+"F10.wireOp",EDGE,"E322")])],"isStart":false})});
            var sketch = newSketch(context, id + "F12", { "sketchPlane" : qUnion([Q0])});
            skPoint(sketch, "E348", {"position": v(-5.1, -7.2) * mm});
            skArc(sketch, "E349", {"start": v(4.6, -7.2) * mm, "mid": v(3.7, -3.13) * mm, "end": v(1.2, 0.19) * mm});
            skArc(sketch, "E350", {"start": v(9.1, -7.2) * mm, "mid": v(8.1, -1.98) * mm, "end": v(5.26, 2.51) * mm});
            skArc(sketch, "E351", {"start": v(6.6, -7.2) * mm, "mid": v(5.23, -1.7) * mm, "end": v(1.44, 2.51) * mm});
            skArc(sketch, "E352", {"start": v(2.74, -7.2) * mm, "mid": v(2.34, -4.73) * mm, "end": v(1.2, -2.52) * mm});
            skArc(sketch, "E353", {"start": v(-1.96, -7.2) * mm, "mid": v(-5.1, -4.04) * mm, "end": v(-8.26, -7.2) * mm});
            skLineSegment(sketch, "E354", {"start": v(-8.26, -7.2) * mm, "end": v(-1.96, -7.2) * mm});
            skArc(sketch, "E355", {"start": v(-0.26, -7.2) * mm, "mid": v(-5.1, -2.34) * mm, "end": v(-9.96, -7.2) * mm});
            skLineSegment(sketch, "E356", {"start": v(-16.82, -7.2) * mm, "end": v(-19.32, -7.2) * mm});
            skLineSegment(sketch, "E357", {"start": v(-14.82, -7.2) * mm, "end": v(-12.96, -7.2) * mm});
            skLineSegment(sketch, "E358", {"start": v(2.74, -7.2) * mm, "end": v(4.6, -7.2) * mm});
            skLineSegment(sketch, "E359", {"start": v(6.6, -7.2) * mm, "end": v(9.1, -7.2) * mm});
            skLineSegment(sketch, "E360", {"start": v(-0.26, -3.76) * mm, "end": v(-0.26, -7.2) * mm});
            skLineSegment(sketch, "E361", {"start": v(-0.26, -7.2) * mm, "end": v(-0.26, -3.76) * mm});
            skLineSegment(sketch, "E362", {"start": v(-9.96, -7.2) * mm, "end": v(-9.96, -3.14) * mm});
            skArc(sketch, "E363.trimOffspring", {"start": v(-0.26, -3.76) * mm, "mid": v(-4.96, -1.13) * mm, "end": v(-9.96, -3.14) * mm});
            skLineSegment(sketch, "E364", {"start": v(-9.96, -1.03) * mm, "end": v(-9.96, 1.21) * mm});
            skLineSegment(sketch, "E365", {"start": v(-11.41, -2.52) * mm, "end": v(-11.41, 0.19) * mm});
            skArc(sketch, "E366.trimOffspring", {"start": v(-11.41, -2.52) * mm, "mid": v(-12.56, -4.73) * mm, "end": v(-12.96, -7.2) * mm});
            skArc(sketch, "E367.trimOffspring", {"start": v(-11.41, 0.19) * mm, "mid": v(-13.93, -3.13) * mm, "end": v(-14.82, -7.2) * mm});
            skLineSegment(sketch, "E368", {"start": v(-0.26, 1.21) * mm, "end": v(-0.26, -1.03) * mm});
            skLineSegment(sketch, "E369", {"start": v(1.2, 0.19) * mm, "end": v(1.2, -2.52) * mm});
            skArc(sketch, "E370.trimOffspring", {"start": v(-0.26, -1.03) * mm, "mid": v(-5.1, 0.65) * mm, "end": v(-9.96, -1.03) * mm});
            skArc(sketch, "E371.trimOffspring", {"start": v(-0.26, 1.21) * mm, "mid": v(-5.1, 2.51) * mm, "end": v(-9.96, 1.21) * mm});
            skLineSegment(sketch, "E372", {"start": v(5.26, 2.51) * mm, "end": v(1.44, 2.51) * mm});
            skLineSegment(sketch, "E373", {"start": v(1.2, 5.54) * mm, "end": v(1.2, 4.03) * mm});
            skLineSegment(sketch, "E374", {"start": v(1.2, 4.03) * mm, "end": v(3.6, 4.03) * mm});
            skLineSegment(sketch, "E375", {"start": v(-1.8, 4.03) * mm, "end": v(-0.26, 4.03) * mm});
            skLineSegment(sketch, "E376", {"start": v(-0.26, 6.16) * mm, "end": v(-0.26, 4.03) * mm});
            skLineSegment(sketch, "E377", {"start": v(-9.96, 6.16) * mm, "end": v(-9.96, 4.03) * mm});
            skLineSegment(sketch, "E378", {"start": v(-9.96, 4.03) * mm, "end": v(-8.43, 4.03) * mm});
            skLineSegment(sketch, "E379", {"start": v(-15.48, 2.51) * mm, "end": v(-11.65, 2.51) * mm});
            skLineSegment(sketch, "E380", {"start": v(-11.41, 4.03) * mm, "end": v(-11.41, 5.54) * mm});
            skLineSegment(sketch, "E381", {"start": v(-11.41, 4.03) * mm, "end": v(-13.82, 4.03) * mm});
            skArc(sketch, "E382.trimOffspring", {"start": v(-15.48, 2.51) * mm, "mid": v(-18.32, -1.98) * mm, "end": v(-19.32, -7.2) * mm});
            skArc(sketch, "E383.trimOffspring", {"start": v(-11.65, 2.51) * mm, "mid": v(-15.45, -1.7) * mm, "end": v(-16.82, -7.2) * mm});
            skArc(sketch, "E384.trimOffspring", {"start": v(-1.8, 4.03) * mm, "mid": v(-5.1, 4.51) * mm, "end": v(-8.43, 4.03) * mm});
            skArc(sketch, "E385.trimOffspring", {"start": v(3.6, 4.03) * mm, "mid": v(-5.1, 7.01) * mm, "end": v(-13.82, 4.03) * mm});
            skArc(sketch, "E386", {"start": v(6.44, 4.03) * mm, "mid": v(4, 6.1) * mm, "end": v(1.2, 7.63) * mm, "construction": true});
            skLineSegment(sketch, "E387", {"start": v(-16.66, 4.03) * mm, "end": v(-19.6, 4.03) * mm, "construction": true});
            skLineSegment(sketch, "E388", {"start": v(-11.41, 9.94) * mm, "end": v(-11.41, 7.63) * mm, "construction": true});
            skLineSegment(sketch, "E389", {"start": v(-9.96, 8.16) * mm, "end": v(-9.96, 10.4) * mm, "construction": true});
            skLineSegment(sketch, "E390", {"start": v(-0.26, 8.16) * mm, "end": v(-0.26, 10.36) * mm, "construction": true});
            skLineSegment(sketch, "E391", {"start": v(1.2, 7.63) * mm, "end": v(1.2, 10.06) * mm});
            skLineSegment(sketch, "E392", {"start": v(7.74, 2.51) * mm, "end": v(10.45, 2.51) * mm, "construction": true});
            skLineSegment(sketch, "E393", {"start": v(10.9, 1.74) * mm, "end": v(10.9, -5.42) * mm, "construction": true});
            skLineSegment(sketch, "E394", {"start": v(-21.12, 2.51) * mm, "end": v(-17.96, 2.51) * mm, "construction": true});
            skLineSegment(sketch, "E395", {"start": v(-21.12, 2.51) * mm, "end": v(-21.12, -5.44) * mm, "construction": true});
            skArc(sketch, "E396.trimOffspring", {"start": v(-17.96, 2.51) * mm, "mid": v(-20.08, -1.25) * mm, "end": v(-21.12, -5.44) * mm, "construction": true});
            skArc(sketch, "E397.trimOffspring", {"start": v(-11.41, 7.63) * mm, "mid": v(-14.22, 6.1) * mm, "end": v(-16.66, 4.03) * mm, "construction": true});
            skArc(sketch, "E398.trimOffspring", {"start": v(-0.26, 10.36) * mm, "mid": v(-5.1, 11.03) * mm, "end": v(-9.96, 10.4) * mm, "construction": true});
            skArc(sketch, "E399.trimOffspring", {"start": v(-0.26, 8.16) * mm, "mid": v(-5.1, 8.91) * mm, "end": v(-9.96, 8.16) * mm, "construction": true});
            skArc(sketch, "E400.trimOffspring", {"start": v(-11.41, 9.94) * mm, "mid": v(-15.92, 7.56) * mm, "end": v(-19.6, 4.03) * mm, "construction": true});
            skArc(sketch, "E401.trimOffspring", {"start": v(9.39, 4.03) * mm, "mid": v(5.71, 7.62) * mm, "end": v(1.2, 10.06) * mm, "construction": true});
            skArc(sketch, "E402", {"start": v(7.74, 2.51) * mm, "mid": v(9.86, -1.24) * mm, "end": v(10.9, -5.42) * mm, "construction": true});
            skLineSegment(sketch, "E403", {"start": v(6.44, 4.03) * mm, "end": v(9.39, 4.03) * mm, "construction": true});
            skArc(sketch, "E404", {"start": v(10.45, 2.51) * mm, "mid": v(10.68, 2.13) * mm, "end": v(10.9, 1.74) * mm, "construction": true});
            skLineSegment(sketch, "E405", {"start": v(13.23, -7.2) * mm, "end": v(12.35, -7.2) * mm, "construction": true});
            skLineSegment(sketch, "E406", {"start": v(12.35, -7.2) * mm, "end": v(12.35, -1.6) * mm, "construction": true});
            skArc(sketch, "E407.trimOffspring", {"start": v(12.35, -1.6) * mm, "mid": v(13, -4.36) * mm, "end": v(13.23, -7.2) * mm, "construction": true});
            skSolve(sketch);
        }
        {
            var Q0;
            Q0 = qSketchRegion(id + "F12", true);
            extrude(context, id + "F13", {"entities" : qUnion([Q0]), "operationType" : NewBodyOperationType.REMOVE, "endBound" : BoundingType.THROUGH_ALL, "oppositeDirection" : true, "depth" : 25 * mm, "offsetDistance" : 25 * mm});
        }
    });
